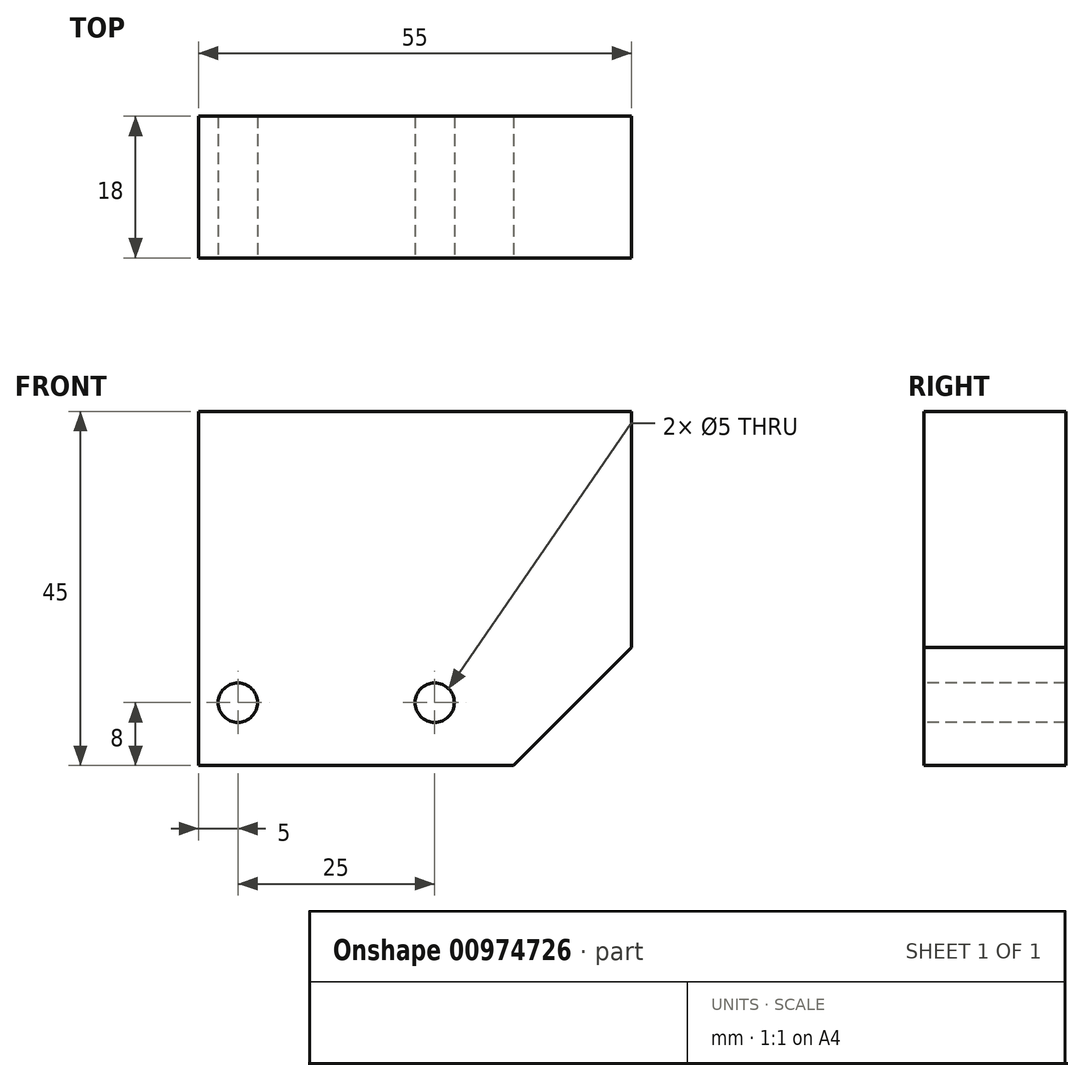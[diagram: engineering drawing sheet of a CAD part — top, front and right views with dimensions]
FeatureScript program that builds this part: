
annotation { "Feature Type Name" : "Feature", "Feature Type Description" : "" }
export const myFeature = defineFeature(function(context is Context, id is Id, definition is map)
    precondition{}
    {
        {
            var Q0;
            Q0=qCreatedBy(makeId("Front.planeOp"),FACE);
            var sketch = newSketch(context, id + "F0", { "sketchPlane" : qUnion([Q0])});
            skLineSegment(sketch, "E0.bottom", {"start": v(0, 0) * mm, "end": v(55, 0) * mm});
            skLineSegment(sketch, "E0.top", {"start": v(0, 45) * mm, "end": v(55, 45) * mm});
            skLineSegment(sketch, "E0.left", {"start": v(0, 0) * mm, "end": v(0, 45) * mm});
            skLineSegment(sketch, "E0.right", {"start": v(55, 0) * mm, "end": v(55, 45) * mm});
            skSolve(sketch);
        }
        {
            var Q0;
            Q0=makeQuery(id+"F0.imprint","IMPRINT",FACE,{"disambiguationData":[TD([[makeQuery(id+"F0.imprint","IMPRINT",EDGE,{"derivedFrom":sQuery(id+"F0.wireOp",EDGE,"E0.bottom")}),1.0]])]});
            extrude(context, id + "F1", {"entities" : qUnion([Q0]), "depth" : 18 * mm, "offsetDistance" : 25 * mm});
        }
        {
            var Q0;
            Q0=makeQuery(id+"F1.opExtrude","CAP_FACE",FACE,{"disambiguationData":[OSD([sQuery(id+"F0.wireOp",EDGE,"E0.bottom"),sQuery(id+"F0.wireOp",EDGE,"E0.top"),sQuery(id+"F0.wireOp",EDGE,"E0.left"),sQuery(id+"F0.wireOp",EDGE,"E0.right")])],"isStart":false});
            var sketch = newSketch(context, id + "F2", { "sketchPlane" : qUnion([Q0])});
            skPoint(sketch, "E1", {"position": v(5, 8) * mm});
            skPoint(sketch, "E2", {"position": v(30, 8) * mm});
            skSolve(sketch);
        }
        {
            var Q0;
            Q0=makeQuery(id+"F1.opExtrude","SWEPT_EDGE",EDGE,{"disambiguationData":[OSD([sQuery(id+"F0.wireOp",EDGE,"E0.bottom"),sQuery(id+"F0.wireOp",EDGE,"E0.right")])]});
            chamfer(context, id + "F3", {"entities" : qUnion([Q0]), "width" : 15 * mm, "tangentPropagation" : true});
        }
        {
            var Q0;
            Q0=sQuery(id+"F2.wireOp",VERTEX,"E2");
            var Q1;
            Q1=sQuery(id+"F2.wireOp",VERTEX,"E1");
            var Q2;
            Q2=makeQuery(id+"F1.opExtrude","SWEPT_BODY",BODY,{"disambiguationData":[OSD([sQuery(id+"F0.wireOp",EDGE,"E0.bottom"),sQuery(id+"F0.wireOp",EDGE,"E0.top"),sQuery(id+"F0.wireOp",EDGE,"E0.left"),sQuery(id+"F0.wireOp",EDGE,"E0.right")])]});
            hole(context, id + "F4", {"style" : HoleStyle.SIMPLE, "endStyle" : HoleEndStyle.THROUGH, "standardTappedOrClearance" : lookupTablePath({ "standard" : "ISO", "size" : "5", "type" : "Drilled" }), "standardBlindInLast" : lookupTablePath({ "standard" : "ISO", "size" : "5", "type" : "Drilled" }), "holeDiameter" : 5 * mm, "majorDiameter" : 4 * mm, "isTappedThrough" : true, "tappedDepth" : 12.6 * mm, "tapClearance" : 3, "startFromSketch" : true, "locations" : qUnion([Q0, Q1]), "scope" : qUnion([Q2])});
        }
    });
